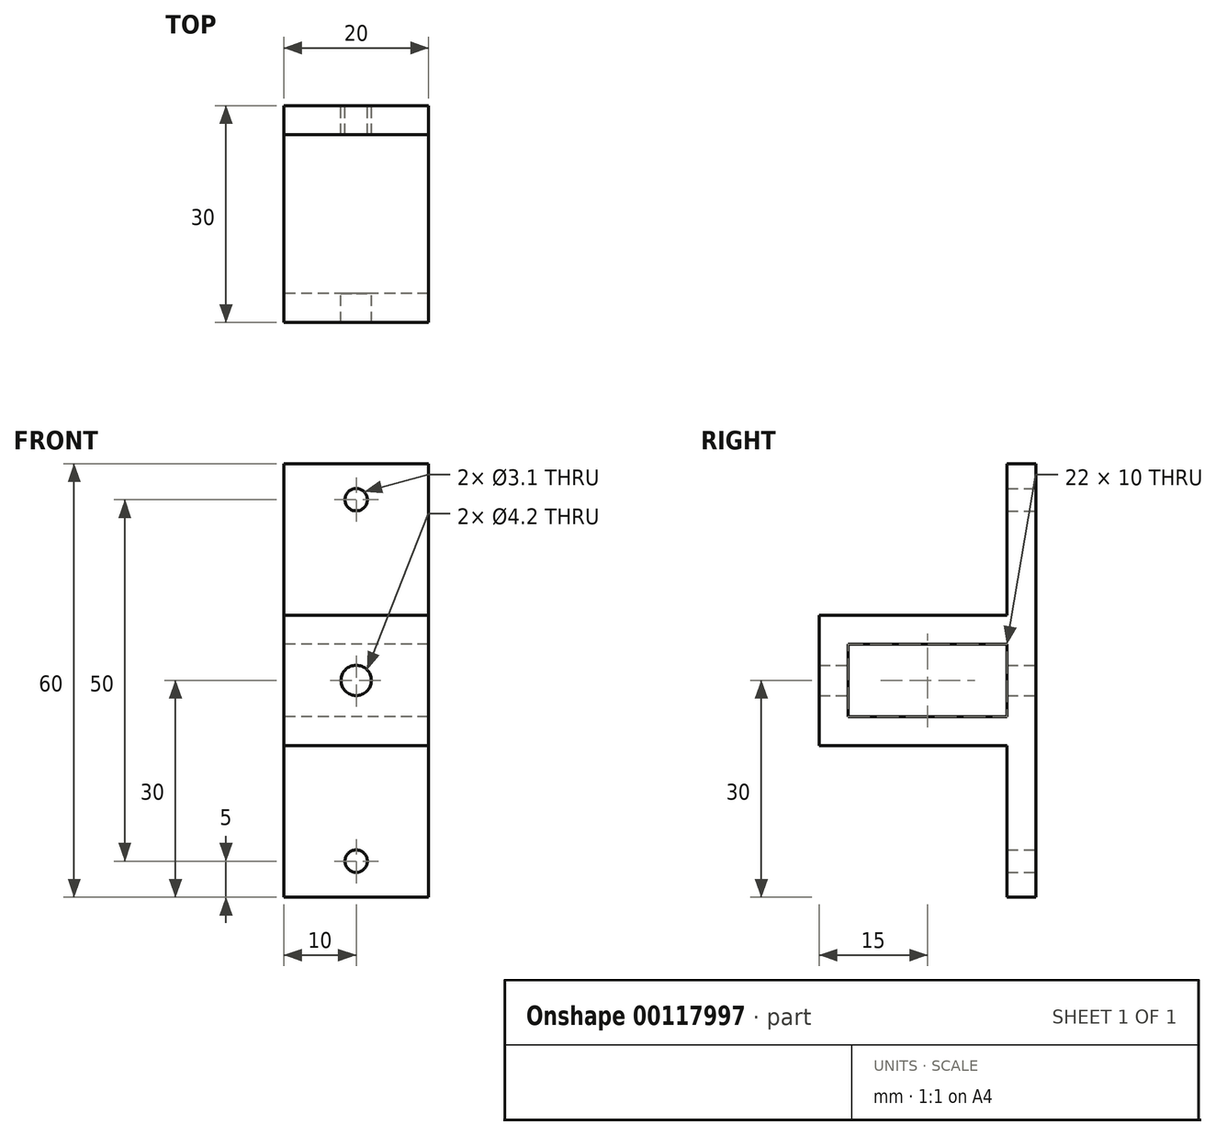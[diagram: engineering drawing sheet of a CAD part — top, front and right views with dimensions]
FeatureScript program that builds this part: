
annotation { "Feature Type Name" : "Feature", "Feature Type Description" : "" }
export const myFeature = defineFeature(function(context is Context, id is Id, definition is map)
    precondition{}
    {
        {
            var Q0;
            Q0=qCreatedBy(makeId("Right.planeOp"),FACE);
            var sketch = newSketch(context, id + "F0", { "sketchPlane" : qUnion([Q0])});
            skLineSegment(sketch, "E0", {"start": v(-20, 0) * mm, "end": v(-20, 60) * mm});
            skLineSegment(sketch, "E1", {"start": v(-20, 60) * mm, "end": v(-24, 60) * mm});
            skLineSegment(sketch, "E2", {"start": v(-24, 60) * mm, "end": v(-24, 39) * mm});
            skLineSegment(sketch, "E3", {"start": v(-24, 39) * mm, "end": v(-50, 39) * mm});
            skLineSegment(sketch, "E4", {"start": v(-50, 39) * mm, "end": v(-50, 21) * mm});
            skLineSegment(sketch, "E5", {"start": v(-50, 21) * mm, "end": v(-24, 21) * mm});
            skLineSegment(sketch, "E6", {"start": v(-24, 21) * mm, "end": v(-24, 0) * mm});
            skLineSegment(sketch, "E7", {"start": v(-24, 0) * mm, "end": v(-20, 0) * mm});
            skLineSegment(sketch, "E8.bottom", {"start": v(-24, 35) * mm, "end": v(-46, 35) * mm});
            skLineSegment(sketch, "E8.top", {"start": v(-24, 25) * mm, "end": v(-46, 25) * mm});
            skLineSegment(sketch, "E8.left", {"start": v(-24, 35) * mm, "end": v(-24, 25) * mm});
            skLineSegment(sketch, "E8.right", {"start": v(-46, 35) * mm, "end": v(-46, 25) * mm});
            skLineSegment(sketch, "E9", {"start": v(-24, 21) * mm, "end": v(-24, 25) * mm, "construction": true});
            skLineSegment(sketch, "E10", {"start": v(-24, 35) * mm, "end": v(-24, 39) * mm, "construction": true});
            skLineSegment(sketch, "E11", {"start": v(-46, 35) * mm, "end": v(-50, 35) * mm, "construction": true});
            skSolve(sketch);
        }
        {
            var Q0;
            Q0 = qSketchRegion(id + "F0", true);
            extrude(context, id + "F1", {"entities" : qUnion([Q0]), "depth" : 20 * mm});
        }
        {
            var Q0;
            Q0=makeQuery(id+"F1.opExtrude","SWEPT_FACE",FACE,{"disambiguationData":[OSD([sQuery(id+"F0.wireOp",EDGE,"E0")])]});
            var sketch = newSketch(context, id + "F2", { "sketchPlane" : qUnion([Q0])});
            skLineSegment(sketch, "E12", {"start": v(-10, 60) * mm, "end": v(-10, 39) * mm, "construction": true});
            skLineSegment(sketch, "E13.0", {"start": v(-20, 21) * mm, "end": v(0, 21) * mm, "construction": true});
            skLineSegment(sketch, "E13.1", {"start": v(-20, 0) * mm, "end": v(0, 0) * mm, "construction": true});
            skLineSegment(sketch, "E13.2", {"start": v(-20, 21) * mm, "end": v(0, 21) * mm, "construction": true});
            skLineSegment(sketch, "E13.3", {"start": v(-20, 39) * mm, "end": v(0, 39) * mm, "construction": true});
            skLineSegment(sketch, "E14", {"start": v(-10, 0) * mm, "end": v(-10, 21) * mm, "construction": true});
            skLineSegment(sketch, "E15", {"start": v(-10, 39) * mm, "end": v(-10, 21) * mm, "construction": true});
            skCircle(sketch, "E16", {"center": v(-10, 55) * mm, "radius": 1.55 * mm});
            skCircle(sketch, "E17", {"center": v(-10, 5) * mm, "radius": 1.55 * mm});
            skCircle(sketch, "E18", {"center": v(-10, 30) * mm, "radius": 2.1 * mm});
            skLineSegment(sketch, "E19", {"start": v(4.5, 30) * mm, "end": v(15.68, 30) * mm, "construction": true});
            skSolve(sketch);
        }
        {
            var Q0;
            Q0 = qSketchRegion(id + "F2", true);
            extrude(context, id + "F3", {"entities" : qUnion([Q0]), "operationType" : NewBodyOperationType.REMOVE, "endBound" : BoundingType.THROUGH_ALL, "oppositeDirection" : true, "depth" : 25 * mm});
        }
    });
